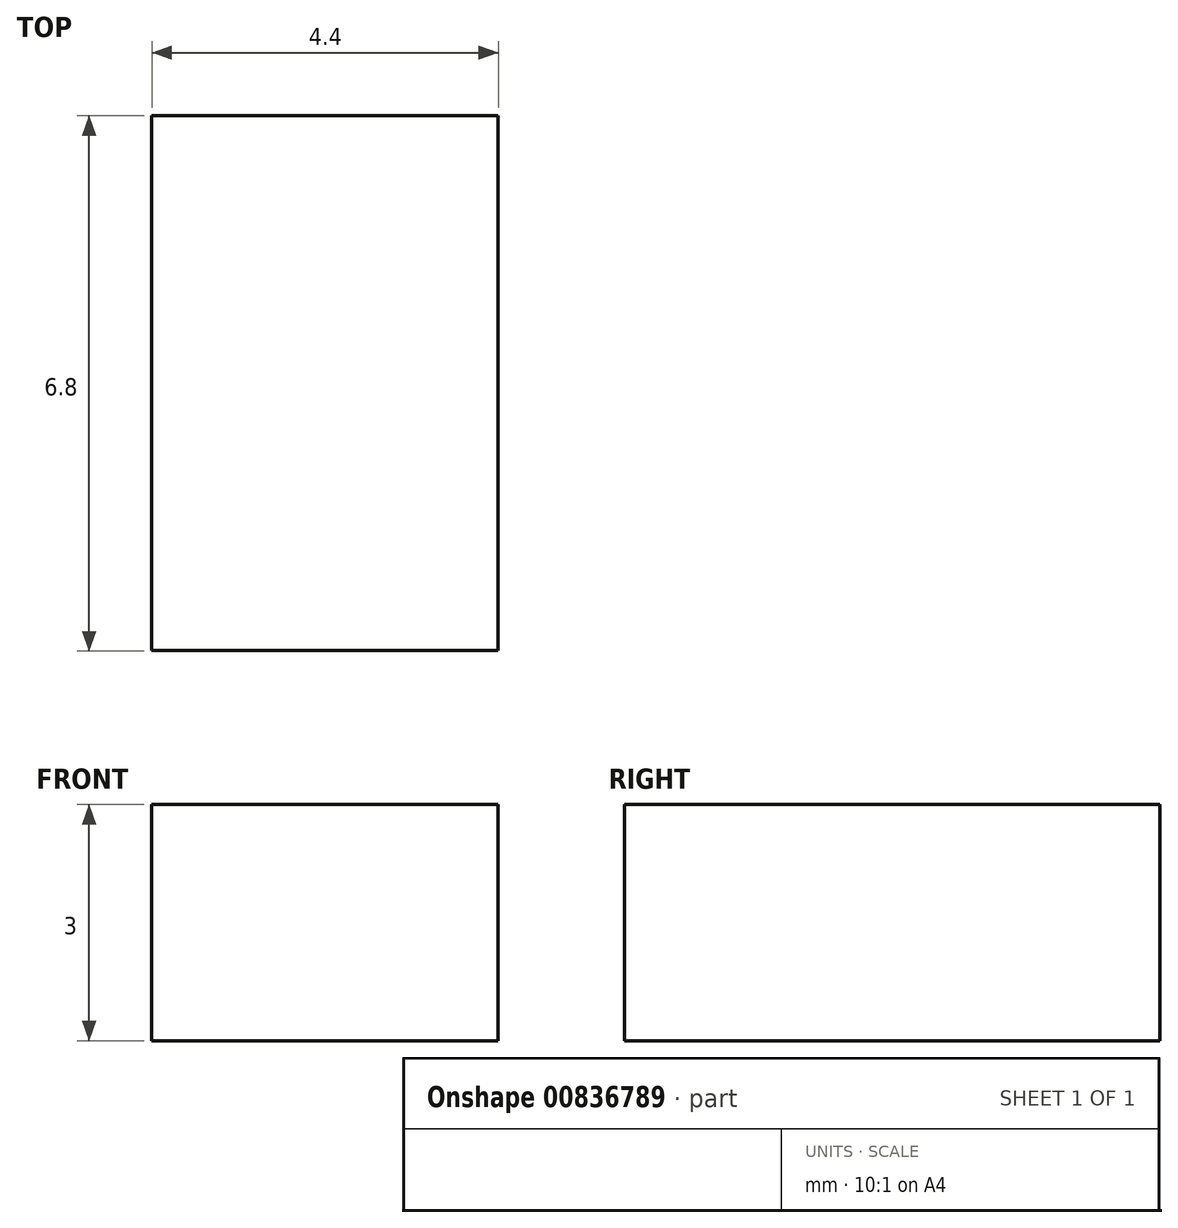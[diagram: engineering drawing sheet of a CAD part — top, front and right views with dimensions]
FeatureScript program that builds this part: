
annotation { "Feature Type Name" : "Feature", "Feature Type Description" : "" }
export const myFeature = defineFeature(function(context is Context, id is Id, definition is map)
    precondition{}
    {
        {
            var Q0;
            Q0=qCreatedBy(makeId("Top.planeOp"),FACE);
            var sketch = newSketch(context, id + "F0", { "sketchPlane" : qUnion([Q0])});
            skLineSegment(sketch, "E0.bottom", {"start": v(2.2, -3.33) * mm, "end": v(-2.2, -3.33) * mm});
            skLineSegment(sketch, "E0.top", {"start": v(2.2, 3.47) * mm, "end": v(-2.2, 3.47) * mm});
            skLineSegment(sketch, "E0.left", {"start": v(2.2, -3.33) * mm, "end": v(2.2, 3.47) * mm});
            skLineSegment(sketch, "E0.right", {"start": v(-2.2, -3.33) * mm, "end": v(-2.2, 3.47) * mm});
            skPoint(sketch, "E0.middle", {"position": v(0, 0.07) * mm});
            skSolve(sketch);
        }
        {
            var Q0;
            Q0 = qSketchRegion(id + "F0", true);
            extrude(context, id + "F1", {"entities" : qUnion([Q0]), "depth" : 3 * mm, "offsetDistance" : 25 * mm});
        }
    });
